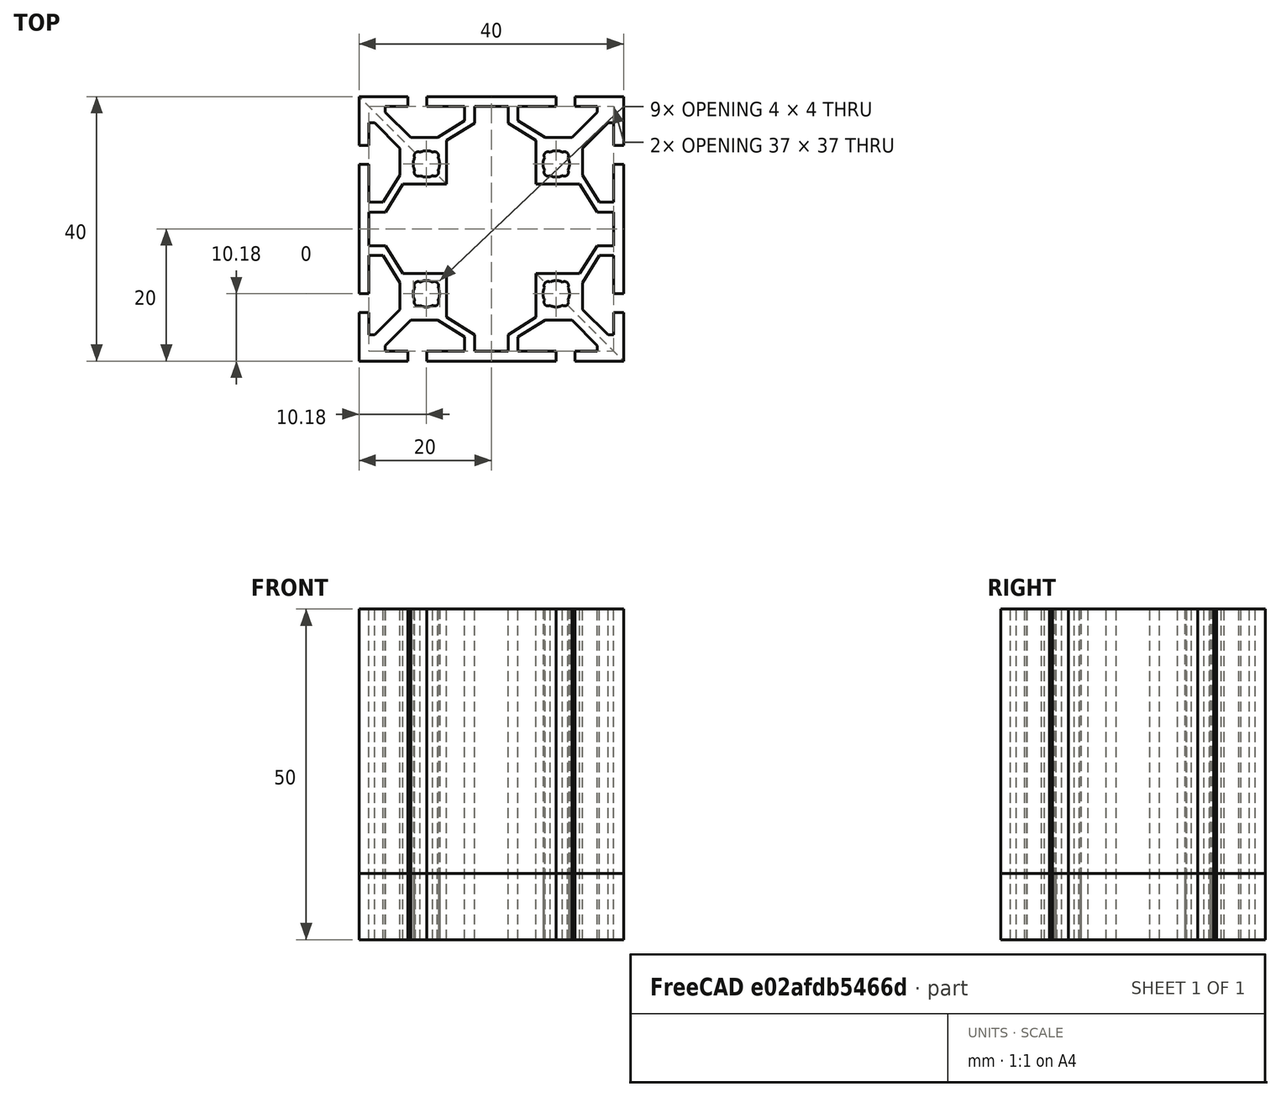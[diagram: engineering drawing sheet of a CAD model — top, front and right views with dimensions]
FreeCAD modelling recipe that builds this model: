
FCSTD DOCUMENT  (FreeCAD 0.18R16093 (Git))
Label: Profile 20-4040
License: All rights reserved
LicenseURL: http://en.wikipedia.org/wiki/All_rights_reserved
objects: PartDesign::Body×3, Sketcher::SketchObject×2, PartDesign::Pad×2, PartDesign::Mirrored×2, PartDesign::PolarPattern×1, PartDesign::FeatureBase×1, PartDesign::Boolean×1, App::Part×1
note: 14 computed .brp shape members not serialized (recipe doc carries the construction recipe); baked Part::Feature solids carry a one-line shape summary decoded from their .brp

FEATURE [Sketcher::SketchObject] Sketch
  MapMode = 5
  Support = -> [XY_Plane001]
  sketch-geometry (38):
    g0: LineSegment [constr] StartX=-22.5 StartY=-22.5 StartZ=0 EndX=22.5 EndY=-22.5 EndZ=0
    g1: LineSegment [constr] StartX=22.5 StartY=-22.5 StartZ=0 EndX=22.5 EndY=22.5 EndZ=0
    g2: LineSegment [constr] StartX=22.5 StartY=22.5 StartZ=0 EndX=-22.5 EndY=22.5 EndZ=0
    g3: LineSegment [constr] StartX=-22.5 StartY=22.5 StartZ=0 EndX=-22.5 EndY=-22.5 EndZ=0
    g4: LineSegment [constr] StartX=-22.5 StartY=22.5 StartZ=0 EndX=0 EndY=0 EndZ=0
    g5: LineSegment [constr] StartX=0 StartY=0 StartZ=0 EndX=22.5 EndY=-22.5 EndZ=0
    g6: LineSegment StartX=13.369 StartY=6.77383 StartZ=0 EndX=15.9987 EndY=2.5456 EndZ=0
    g7: LineSegment StartX=15.9987 StartY=2.5456 StartZ=0 EndX=18.5 EndY=2.5456 EndZ=0
    g8: LineSegment StartX=18.5 StartY=2.5456 StartZ=0 EndX=18.5 EndY=0 EndZ=0
    g9: LineSegment StartX=18.5 StartY=0 StartZ=0 EndX=20 EndY=0 EndZ=0
    g10: LineSegment StartX=20 StartY=0 StartZ=0 EndX=20 EndY=9.77979 EndZ=0
    g11: LineSegment StartX=20 StartY=9.77979 StartZ=0 EndX=18.5 EndY=9.77979 EndZ=0
    g12: LineSegment StartX=18.5 StartY=9.77979 StartZ=0 EndX=18.5 EndY=4.0456 EndZ=0
    g13: LineSegment StartX=18.5 StartY=4.0456 StartZ=0 EndX=16.3382 EndY=4.0456 EndZ=0
    g14: LineSegment StartX=16.3382 StartY=4.0456 StartZ=0 EndX=13.8 EndY=8.12685 EndZ=0
    g15: LineSegment StartX=13.8 StartY=8.12685 StartZ=0 EndX=13.8 EndY=12.191 EndZ=0
    g16: LineSegment StartX=13.8 StartY=12.191 StartZ=0 EndX=17.6446 EndY=16.0356 EndZ=0
    g17: LineSegment StartX=17.6446 StartY=16.0356 StartZ=0 EndX=18.5 EndY=16.0356 EndZ=0
    g18: LineSegment StartX=18.5 StartY=16.0356 StartZ=0 EndX=18.5 EndY=12.63 EndZ=0
    g19: LineSegment StartX=18.5 StartY=12.63 StartZ=0 EndX=20 EndY=12.63 EndZ=0
    g20: LineSegment StartX=20 StartY=12.63 StartZ=0 EndX=20 EndY=20 EndZ=0
    g21: LineSegment StartX=13.369 StartY=6.77383 StartZ=0 EndX=6.77383 EndY=6.77383 EndZ=0
    g22: LineSegment StartX=6.77383 StartY=6.77383 StartZ=0 EndX=8.14622 EndY=8.14622 EndZ=0
    g23: LineSegment [constr] StartX=8.57049 StartY=11.0705 StartZ=0 EndX=11.0705 EndY=11.0705 EndZ=0
    g24: LineSegment [constr] StartX=11.0705 StartY=11.0705 StartZ=0 EndX=11.0705 EndY=8.57049 EndZ=0
    g25: LineSegment [constr] StartX=11.0705 StartY=8.57049 StartZ=0 EndX=8.57049 EndY=8.57049 EndZ=0
    g26: LineSegment [constr] StartX=8.57049 StartY=8.57049 StartZ=0 EndX=8.57049 EndY=11.0705 EndZ=0
    g27: LineSegment [constr] StartX=8.57049 StartY=11.0705 StartZ=0 EndX=9.82049 EndY=9.82049 EndZ=0
    g28: LineSegment [constr] StartX=9.82049 StartY=9.82049 StartZ=0 EndX=11.0705 EndY=8.57049 EndZ=0
    g29: LineSegment StartX=11.4947 StartY=11.4947 StartZ=0 EndX=20 EndY=20 EndZ=0
    g30: LineSegment [constr] StartX=18.5 StartY=4.0456 StartZ=0 EndX=18.5 EndY=2.5456 EndZ=0
    g31: LineSegment [constr] StartX=11.4947 StartY=11.4947 StartZ=0 EndX=11.0705 EndY=11.0705 EndZ=0
    g32: LineSegment [constr] StartX=8.57049 StartY=8.57049 StartZ=0 EndX=8.14622 EndY=8.14622 EndZ=0
    g33: ArcOfCircle CenterX=11.0705 CenterY=8.57049 CenterZ=0 NormalX=0 NormalY=0 NormalZ=1 AngleXU=0 Radius=0.6 StartAngle=4.17221 EndAngle=6.82336
    g34: ArcOfCircle CenterX=8.57049 CenterY=8.57049 CenterZ=0 NormalX=0 NormalY=0 NormalZ=1 AngleXU=0 Radius=0.6 StartAngle=3.92699 EndAngle=5.25256
    g35: ArcOfCircle CenterX=11.0705 CenterY=11.0705 CenterZ=0 NormalX=0 NormalY=0 NormalZ=1 AngleXU=0 Radius=0.6 StartAngle=5.74301 EndAngle=7.06858
    g36: ArcOfCircle CenterX=9.82049 CenterY=9.82049 CenterZ=0 NormalX=0 NormalY=0 NormalZ=1 AngleXU=0 Radius=2 StartAngle=5.79309 EndAngle=6.77329
    g37: ArcOfCircle CenterX=9.82049 CenterY=9.82049 CenterZ=0 NormalX=0 NormalY=0 NormalZ=1 AngleXU=0 Radius=2 StartAngle=4.22229 EndAngle=5.20249
  constraints (99):
    c: Horizontal(g0)
    c: Coincident(g0,g1)
    c: Vertical(g1)
    c: Coincident(g1,g2)
    c: Horizontal(g2)
    c: Coincident(g2,g3)
    c: Coincident(g3,g0)
    c: Vertical(g3)
    c: Coincident(g2,g4)
    c: Coincident(g4,g-1)
    c: Coincident(g4,g5)
    c: Coincident(g5,g0)
    c: Parallel(g4,g5)
    c: Equal(g1,g2)
    c: DistanceX(g2,g2) = 45
    c: Coincident(g6,g7)
    c: Coincident(g7,g8)
    c: PointOnObject(g8,g-1)
    c: Coincident(g8,g9)
    c: PointOnObject(g9,g-1)
    c: Coincident(g9,g10)
    c: Vertical(g10)
    c: Coincident(g10,g11)
    c: Horizontal(g11)
    c: Coincident(g11,g12)
    c: Vertical(g12)
    c: Coincident(g12,g13)
    c: Coincident(g13,g14)
    c: Coincident(g14,g15)
    c: Vertical(g15)
    c: Coincident(g15,g16)
    c: Coincident(g16,g17)
    c: Coincident(g17,g18)
    c: Coincident(g18,g19)
    c: Horizontal(g19)
    c: Coincident(g19,g20)
    c: Vertical(g20)
    c: Coincident(g6,g21)
    c: Horizontal(g21)
    c: Coincident(g21,g22)
    c: Coincident(g29,g20)
    c: Coincident(g24,g25)
    c: Coincident(g26,g23)
    c: Horizontal(g23)
    c: Horizontal(g25)
    c: Vertical(g24)
    c: Vertical(g26)
    c: Coincident(g23,g27)
    c: Coincident(g27,g28)
    c: Coincident(g28,g24)
    c: Equal(g28,g27)
    c: Vertical(g18)
    c: Vertical(g8)
    c: Horizontal(g13)
    c: Horizontal(g7)
    c: Horizontal(g17)
    c: DistanceX(g-1,g20) = 20
    c: DistanceX(g14,g11) = 4.7
    c: Vertical(g12,g7)
    c: DistanceX(g9,g9) = 1.5
    c: Vertical(g19,g10)
    c: Parallel(g16,g29)
    c: Equal(g19,g9)
    c: DistanceY(g20,g20) = 7.37
    c: DistanceY(g12,g17) = 11.99
    c: Parallel(g14,g6)
    c: Coincident(g30,g12)
    c: Coincident(g30,g7)
    c: Equal(g9,g30)
    c: Coincident(g24,g23)
    c: Coincident(g26,g25)
    c: Parallel(g28,g27)
    c: Parallel(g22,g29)
    c: DistanceY(g-1,g20) = 20
    c: Coincident(g31,g23)
    c: Coincident(g32,g25)
    c: Equal(g31,g32)
    c: Parallel(g32,g22)
    c: Equal(g24,g25)
    c: Coincident(g33,g24)
    c: Coincident(g34,g25)
    c: Coincident(g35,g23)
    c: Coincident(g36,g35)
    c: Coincident(g29,g35)
    c: Coincident(g22,g34)
    c: Coincident(g29,g31)
    c: Coincident(g32,g22)
    c: Coincident(g33,g36)
    c: Equal(g33,g34)
    c: Radius(g35) = 0.6
    c: DistanceX(g25,g25) = 2.5
    c: Parallel(g31,g29)
    c: Coincident(g37,g27)
    c: Coincident(g37,g33)
    c: Coincident(g37,g34)
    c: Equal(g36,g37)
    c: Radius(g36) = 2
    c: Coincident(g37,g36)
    c: Angle(g29,g20) = 0.785398
FEATURE [PartDesign::Pad] Pad
  Length = 10
  Length2 = 100
  Profile = -> Sketch
  Refine = true
  Type = 0
FEATURE [PartDesign::Mirrored] Mirrored
  BaseFeature = -> Pad
  MirrorPlane = -> Pad [Face19]
  Originals = -> [Pad]
  Refine = true
FEATURE [PartDesign::PolarPattern] PolarPattern
  Angle = 90
  Axis = -> Sketch [N_Axis]
  BaseFeature = -> Mirrored
  Occurrences = 2
  Originals = -> [Pad]
  Refine = true
FEATURE [PartDesign::Mirrored] Mirrored001
  BaseFeature = -> PolarPattern
  MirrorPlane = -> XZ_Plane001
  Originals = -> [Pad]
  Refine = true
FEATURE [PartDesign::FeatureBase] Clone
  BaseFeature = -> Mirrored001
  Placement = pos=(0,0,0) rot=(0,0,1;3.14159rad)
FEATURE [PartDesign::Body] Body001
  BaseFeature = -> Mirrored001
  Group = -> [Clone]
  Origin = -> Origin002
  Tip = -> Clone
FEATURE [PartDesign::Boolean] Boolean
  BaseFeature = -> Mirrored001
  Group = -> [Body001]
  Refine = true
  Type = 0
FEATURE [PartDesign::Body] Body
  Group = -> [Sketch,Pad,Mirrored,PolarPattern,Mirrored001,Boolean]
  Origin = -> Origin001
  Tip = -> Boolean
FEATURE [Sketcher::SketchObject] Sketch001
  sketch-geometry (151):
    g0: LineSegment StartX=-12.63 StartY=20 StartZ=0 EndX=-20 EndY=20 EndZ=0
    g1: LineSegment StartX=-12.63 StartY=18.5 StartZ=0 EndX=-12.63 EndY=20 EndZ=0
    g2: LineSegment StartX=-16.0356 StartY=18.5 StartZ=0 EndX=-12.63 EndY=18.5 EndZ=0
    g3: LineSegment StartX=-16.0356 StartY=17.6446 StartZ=0 EndX=-16.0356 EndY=18.5 EndZ=0
    g4: LineSegment StartX=-12.191 StartY=13.8 StartZ=0 EndX=-16.0356 EndY=17.6446 EndZ=0
    g5: LineSegment StartX=-8.12685 StartY=13.8 StartZ=0 EndX=-12.191 EndY=13.8 EndZ=0
    g6: LineSegment StartX=-4.0456 StartY=16.3382 StartZ=0 EndX=-8.12685 EndY=13.8 EndZ=0
    g7: LineSegment StartX=-4.0456 StartY=18.5 StartZ=0 EndX=-4.0456 EndY=16.3382 EndZ=0
    g8: LineSegment StartX=-9.77979 StartY=18.5 StartZ=0 EndX=-4.0456 EndY=18.5 EndZ=0
    g9: LineSegment StartX=-9.77979 StartY=20 StartZ=0 EndX=-9.77979 EndY=18.5 EndZ=0
    g10: LineSegment StartX=-9.77979 StartY=20 StartZ=0 EndX=9.77979 EndY=20 EndZ=0
    g11: LineSegment StartX=9.77979 StartY=20 StartZ=0 EndX=9.77979 EndY=18.5 EndZ=0
    g12: LineSegment StartX=9.77979 StartY=18.5 StartZ=0 EndX=4.0456 EndY=18.5 EndZ=0
    g13: LineSegment StartX=4.0456 StartY=18.5 StartZ=0 EndX=4.0456 EndY=16.3382 EndZ=0
    g14: LineSegment StartX=4.0456 StartY=16.3382 StartZ=0 EndX=8.12685 EndY=13.8 EndZ=0
    g15: LineSegment StartX=8.12685 StartY=13.8 StartZ=0 EndX=12.191 EndY=13.8 EndZ=0
    g16: LineSegment StartX=12.191 StartY=13.8 StartZ=0 EndX=16.0356 EndY=17.6446 EndZ=0
    g17: LineSegment StartX=16.0356 StartY=17.6446 StartZ=0 EndX=16.0356 EndY=18.5 EndZ=0
    g18: LineSegment StartX=16.0356 StartY=18.5 StartZ=0 EndX=12.63 EndY=18.5 EndZ=0
    g19: LineSegment StartX=12.63 StartY=18.5 StartZ=0 EndX=12.63 EndY=20 EndZ=0
    g20: LineSegment StartX=12.63 StartY=20 StartZ=0 EndX=20 EndY=20 EndZ=0
    g21: LineSegment StartX=20 StartY=12.63 StartZ=0 EndX=20 EndY=20 EndZ=0
    g22: LineSegment StartX=18.5 StartY=12.63 StartZ=0 EndX=20 EndY=12.63 EndZ=0
    g23: LineSegment StartX=18.5 StartY=16.0356 StartZ=0 EndX=18.5 EndY=12.63 EndZ=0
    g24: LineSegment StartX=17.6446 StartY=16.0356 StartZ=0 EndX=18.5 EndY=16.0356 EndZ=0
    g25: LineSegment StartX=13.8 StartY=12.191 StartZ=0 EndX=17.6446 EndY=16.0356 EndZ=0
    g26: LineSegment StartX=13.8 StartY=8.12685 StartZ=0 EndX=13.8 EndY=12.191 EndZ=0
    g27: LineSegment StartX=16.3382 StartY=4.0456 StartZ=0 EndX=13.8 EndY=8.12685 EndZ=0
    g28: LineSegment StartX=18.5 StartY=4.0456 StartZ=0 EndX=16.3382 EndY=4.0456 EndZ=0
    g29: LineSegment StartX=18.5 StartY=9.77979 StartZ=0 EndX=18.5 EndY=4.0456 EndZ=0
    g30: LineSegment StartX=20 StartY=9.77979 StartZ=0 EndX=18.5 EndY=9.77979 EndZ=0
    g31: LineSegment StartX=20 StartY=9.77979 StartZ=0 EndX=20 EndY=-9.77979 EndZ=0
    g32: LineSegment StartX=20 StartY=-9.77979 StartZ=0 EndX=18.5 EndY=-9.77979 EndZ=0
    g33: LineSegment StartX=18.5 StartY=-9.77979 StartZ=0 EndX=18.5 EndY=-4.0456 EndZ=0
    g34: LineSegment StartX=18.5 StartY=-4.0456 StartZ=0 EndX=16.3382 EndY=-4.0456 EndZ=0
    g35: LineSegment StartX=16.3382 StartY=-4.0456 StartZ=0 EndX=13.8 EndY=-8.12685 EndZ=0
    g36: LineSegment StartX=13.8 StartY=-8.12685 StartZ=0 EndX=13.8 EndY=-12.191 EndZ=0
    g37: LineSegment StartX=13.8 StartY=-12.191 StartZ=0 EndX=17.6446 EndY=-16.0356 EndZ=0
    g38: LineSegment StartX=17.6446 StartY=-16.0356 StartZ=0 EndX=18.5 EndY=-16.0356 EndZ=0
    g39: LineSegment StartX=18.5 StartY=-16.0356 StartZ=0 EndX=18.5 EndY=-12.63 EndZ=0
    g40: LineSegment StartX=18.5 StartY=-12.63 StartZ=0 EndX=20 EndY=-12.63 EndZ=0
    g41: LineSegment StartX=20 StartY=-12.63 StartZ=0 EndX=20 EndY=-20 EndZ=0
    g42: LineSegment StartX=12.63 StartY=-20 StartZ=0 EndX=20 EndY=-20 EndZ=0
    g43: LineSegment StartX=12.63 StartY=-18.5 StartZ=0 EndX=12.63 EndY=-20 EndZ=0
    g44: LineSegment StartX=16.0356 StartY=-18.5 StartZ=0 EndX=12.63 EndY=-18.5 EndZ=0
    g45: LineSegment StartX=16.0356 StartY=-17.6446 StartZ=0 EndX=16.0356 EndY=-18.5 EndZ=0
    g46: LineSegment StartX=12.191 StartY=-13.8 StartZ=0 EndX=16.0356 EndY=-17.6446 EndZ=0
    g47: LineSegment StartX=8.12685 StartY=-13.8 StartZ=0 EndX=12.191 EndY=-13.8 EndZ=0
    g48: LineSegment StartX=4.0456 StartY=-16.3382 StartZ=0 EndX=8.12685 EndY=-13.8 EndZ=0
    g49: LineSegment StartX=4.0456 StartY=-18.5 StartZ=0 EndX=4.0456 EndY=-16.3382 EndZ=0
    g50: LineSegment StartX=9.77979 StartY=-18.5 StartZ=0 EndX=4.0456 EndY=-18.5 EndZ=0
    g51: LineSegment StartX=9.77979 StartY=-20 StartZ=0 EndX=9.77979 EndY=-18.5 EndZ=0
    g52: LineSegment StartX=9.77979 StartY=-20 StartZ=0 EndX=-9.77979 EndY=-20 EndZ=0
    g53: LineSegment StartX=-9.77979 StartY=-20 StartZ=0 EndX=-9.77979 EndY=-18.5 EndZ=0
    g54: LineSegment StartX=-9.77979 StartY=-18.5 StartZ=0 EndX=-4.0456 EndY=-18.5 EndZ=0
    g55: LineSegment StartX=-4.0456 StartY=-18.5 StartZ=0 EndX=-4.0456 EndY=-16.3382 EndZ=0
    g56: LineSegment StartX=-4.0456 StartY=-16.3382 StartZ=0 EndX=-8.12685 EndY=-13.8 EndZ=0
    g57: LineSegment StartX=-8.12685 StartY=-13.8 StartZ=0 EndX=-12.191 EndY=-13.8 EndZ=0
    g58: LineSegment StartX=-12.191 StartY=-13.8 StartZ=0 EndX=-16.0356 EndY=-17.6446 EndZ=0
    g59: LineSegment StartX=-16.0356 StartY=-17.6446 StartZ=0 EndX=-16.0356 EndY=-18.5 EndZ=0
    g60: LineSegment StartX=-16.0356 StartY=-18.5 StartZ=0 EndX=-12.63 EndY=-18.5 EndZ=0
    g61: LineSegment StartX=-12.63 StartY=-18.5 StartZ=0 EndX=-12.63 EndY=-20 EndZ=0
    g62: LineSegment StartX=-12.63 StartY=-20 StartZ=0 EndX=-20 EndY=-20 EndZ=0
    g63: LineSegment StartX=-20 StartY=-12.63 StartZ=0 EndX=-20 EndY=-20 EndZ=0
    g64: LineSegment StartX=-18.5 StartY=-12.63 StartZ=0 EndX=-20 EndY=-12.63 EndZ=0
    g65: LineSegment StartX=-18.5 StartY=-16.0356 StartZ=0 EndX=-18.5 EndY=-12.63 EndZ=0
    g66: LineSegment StartX=-17.6446 StartY=-16.0356 StartZ=0 EndX=-18.5 EndY=-16.0356 EndZ=0
    g67: LineSegment StartX=-13.8 StartY=-12.191 StartZ=0 EndX=-17.6446 EndY=-16.0356 EndZ=0
    g68: LineSegment StartX=-13.8 StartY=-8.12685 StartZ=0 EndX=-13.8 EndY=-12.191 EndZ=0
    g69: LineSegment StartX=-16.3382 StartY=-4.0456 StartZ=0 EndX=-13.8 EndY=-8.12685 EndZ=0
    g70: LineSegment StartX=-18.5 StartY=-4.0456 StartZ=0 EndX=-16.3382 EndY=-4.0456 EndZ=0
    g71: LineSegment StartX=-18.5 StartY=-9.77979 StartZ=0 EndX=-18.5 EndY=-4.0456 EndZ=0
    g72: LineSegment StartX=-20 StartY=-9.77979 StartZ=0 EndX=-18.5 EndY=-9.77979 EndZ=0
    g73: LineSegment StartX=-20 StartY=-9.77979 StartZ=0 EndX=-20 EndY=9.77979 EndZ=0
    g74: LineSegment StartX=-20 StartY=9.77979 StartZ=0 EndX=-18.5 EndY=9.77979 EndZ=0
    g75: LineSegment StartX=-18.5 StartY=9.77979 StartZ=0 EndX=-18.5 EndY=4.0456 EndZ=0
    g76: LineSegment StartX=-18.5 StartY=4.0456 StartZ=0 EndX=-16.3382 EndY=4.0456 EndZ=0
    g77: LineSegment StartX=-16.3382 StartY=4.0456 StartZ=0 EndX=-13.8 EndY=8.12685 EndZ=0
    g78: LineSegment StartX=-13.8 StartY=8.12685 StartZ=0 EndX=-13.8 EndY=12.191 EndZ=0
    g79: LineSegment StartX=-13.8 StartY=12.191 StartZ=0 EndX=-17.6446 EndY=16.0356 EndZ=0
    g80: LineSegment StartX=-17.6446 StartY=16.0356 StartZ=0 EndX=-18.5 EndY=16.0356 EndZ=0
    g81: LineSegment StartX=-18.5 StartY=16.0356 StartZ=0 EndX=-18.5 EndY=12.63 EndZ=0
    g82: LineSegment StartX=-18.5 StartY=12.63 StartZ=0 EndX=-20 EndY=12.63 EndZ=0
    g83: LineSegment StartX=-20 StartY=12.63 StartZ=0 EndX=-20 EndY=20 EndZ=0
    g84: LineSegment StartX=-13.369 StartY=-6.77383 StartZ=0 EndX=-6.77383 EndY=-6.77383 EndZ=0
    g85: LineSegment StartX=-6.77383 StartY=-13.369 StartZ=0 EndX=-6.77383 EndY=-6.77383 EndZ=0
    g86: LineSegment StartX=-6.77383 StartY=-13.369 StartZ=0 EndX=-2.5456 EndY=-15.9987 EndZ=0
    g87: LineSegment StartX=-2.5456 StartY=-15.9987 StartZ=0 EndX=-2.5456 EndY=-18.5 EndZ=0
    g88: LineSegment StartX=2.5456 StartY=-18.5 StartZ=0 EndX=-2.5456 EndY=-18.5 EndZ=0
    g89: LineSegment StartX=2.5456 StartY=-15.9987 StartZ=0 EndX=2.5456 EndY=-18.5 EndZ=0
    g90: LineSegment StartX=6.77383 StartY=-13.369 StartZ=0 EndX=2.5456 EndY=-15.9987 EndZ=0
    g91: LineSegment StartX=6.77383 StartY=-13.369 StartZ=0 EndX=6.77383 EndY=-6.77383 EndZ=0
    g92: LineSegment StartX=13.369 StartY=6.77383 StartZ=0 EndX=6.77383 EndY=6.77383 EndZ=0
    g93: LineSegment StartX=13.369 StartY=6.77383 StartZ=0 EndX=15.9987 EndY=2.5456 EndZ=0
    g94: LineSegment StartX=6.77383 StartY=13.369 StartZ=0 EndX=6.77383 EndY=6.77383 EndZ=0
    g95: LineSegment StartX=15.9987 StartY=2.5456 StartZ=0 EndX=18.5 EndY=2.5456 EndZ=0
    g96: LineSegment StartX=6.77383 StartY=13.369 StartZ=0 EndX=2.5456 EndY=15.9987 EndZ=0
    g97: LineSegment StartX=2.5456 StartY=15.9987 StartZ=0 EndX=2.5456 EndY=18.5 EndZ=0
    g98: LineSegment StartX=-2.5456 StartY=18.5 StartZ=0 EndX=2.5456 EndY=18.5 EndZ=0
    g99: LineSegment StartX=-2.5456 StartY=15.9987 StartZ=0 EndX=-2.5456 EndY=18.5 EndZ=0
    g100: LineSegment StartX=-6.77383 StartY=13.369 StartZ=0 EndX=-2.5456 EndY=15.9987 EndZ=0
    g101: LineSegment StartX=-6.77383 StartY=13.369 StartZ=0 EndX=-6.77383 EndY=6.77383 EndZ=0
    g102: LineSegment StartX=18.5 StartY=2.5456 StartZ=0 EndX=18.5 EndY=-2.5456 EndZ=0
    g103: LineSegment StartX=13.369 StartY=-6.77383 StartZ=0 EndX=6.77383 EndY=-6.77383 EndZ=0
    g104: LineSegment StartX=13.369 StartY=-6.77383 StartZ=0 EndX=15.9987 EndY=-2.5456 EndZ=0
    g105: LineSegment StartX=15.9987 StartY=-2.5456 StartZ=0 EndX=18.5 EndY=-2.5456 EndZ=0
    g106: LineSegment StartX=-13.369 StartY=6.77383 StartZ=0 EndX=-6.77383 EndY=6.77383 EndZ=0
    g107: LineSegment StartX=-13.369 StartY=6.77383 StartZ=0 EndX=-15.9987 EndY=2.5456 EndZ=0
    g108: LineSegment StartX=-15.9987 StartY=2.5456 StartZ=0 EndX=-18.5 EndY=2.5456 EndZ=0
    g109: LineSegment StartX=-18.5 StartY=-2.5456 StartZ=0 EndX=-18.5 EndY=2.5456 EndZ=0
    g110: LineSegment StartX=-15.9987 StartY=-2.5456 StartZ=0 EndX=-18.5 EndY=-2.5456 EndZ=0
    g111: LineSegment StartX=-13.369 StartY=-6.77383 StartZ=0 EndX=-15.9987 EndY=-2.5456 EndZ=0
    g112: ArcOfCircle CenterX=-8.57049 CenterY=-8.57049 CenterZ=0 NormalX=0 NormalY=0 NormalZ=1 AngleXU=-1.5708 Radius=0.6 StartAngle=1.03062 EndAngle=2.35619
    g113: ArcOfCircle CenterX=-8.57049 CenterY=-8.57049 CenterZ=0 NormalX=0 NormalY=0 NormalZ=1 AngleXU=3.14159 Radius=0.6 StartAngle=3.92699 EndAngle=5.25256
    g114: ArcOfCircle CenterX=-10 CenterY=-9.99052 CenterZ=0 NormalX=0 NormalY=0 NormalZ=1 AngleXU=3.14159 Radius=2.095 StartAngle=4.1766 EndAngle=5.06528
    g115: ArcOfCircle CenterX=-11.0705 CenterY=-8.57049 CenterZ=0 NormalX=0 NormalY=0 NormalZ=1 AngleXU=3.14159 Radius=0.6 StartAngle=4.17221 EndAngle=6.82336
    g116: ArcOfCircle CenterX=-10 CenterY=-9.99052 CenterZ=0 NormalX=0 NormalY=0 NormalZ=1 AngleXU=3.14159 Radius=2.095 StartAngle=5.75099 EndAngle=6.68341
    g117: ArcOfCircle CenterX=-11.0705 CenterY=-11.0705 CenterZ=0 NormalX=0 NormalY=0 NormalZ=1 AngleXU=-1.5708 Radius=0.6 StartAngle=5.49779 EndAngle=6.82336
    g118: ArcOfCircle CenterX=-11.0705 CenterY=-11.0705 CenterZ=0 NormalX=0 NormalY=0 NormalZ=1 AngleXU=3.14159 Radius=0.6 StartAngle=5.74301 EndAngle=7.06858
    g119: ArcOfCircle CenterX=-10 CenterY=-9.99052 CenterZ=0 NormalX=0 NormalY=0 NormalZ=1 AngleXU=-1.5708 Radius=2.095 StartAngle=5.89427 EndAngle=6.88085
    g120: ArcOfCircle CenterX=-8.57049 CenterY=-11.0705 CenterZ=0 NormalX=0 NormalY=0 NormalZ=1 AngleXU=-1.5708 Radius=0.6 StartAngle=5.74301 EndAngle=8.39416
    g121: ArcOfCircle CenterX=-10 CenterY=-9.99052 CenterZ=0 NormalX=0 NormalY=0 NormalZ=1 AngleXU=-1.5708 Radius=2.095 StartAngle=1.1689 EndAngle=2.10217
    g122: ArcOfCircle CenterX=10 CenterY=-9.99052 CenterZ=0 NormalX=0 NormalY=0 NormalZ=1 AngleXU=0 Radius=2.095 StartAngle=5.88179 EndAngle=6.81528
    g123: ArcOfCircle CenterX=11.0705 CenterY=-8.57049 CenterZ=0 NormalX=0 NormalY=0 NormalZ=1 AngleXU=0 Radius=0.6 StartAngle=5.74301 EndAngle=8.39416
    g124: ArcOfCircle CenterX=10 CenterY=-9.99052 CenterZ=0 NormalX=0 NormalY=0 NormalZ=1 AngleXU=0 Radius=2.095 StartAngle=1.21703 EndAngle=2.10532
    g125: ArcOfCircle CenterX=10 CenterY=-9.99052 CenterZ=0 NormalX=0 NormalY=0 NormalZ=1 AngleXU=-1.5708 Radius=2.095 StartAngle=4.17839 EndAngle=5.11082
    g126: ArcOfCircle CenterX=8.57049 CenterY=-11.0705 CenterZ=0 NormalX=0 NormalY=0 NormalZ=1 AngleXU=-1.5708 Radius=0.6 StartAngle=4.17221 EndAngle=6.82336
    g127: ArcOfCircle CenterX=10 CenterY=-9.99052 CenterZ=0 NormalX=0 NormalY=0 NormalZ=1 AngleXU=-1.5708 Radius=2.095 StartAngle=5.69299 EndAngle=6.679
    g128: ArcOfCircle CenterX=-10 CenterY=9.99052 CenterZ=0 NormalX=0 NormalY=0 NormalZ=1 AngleXU=1.5708 Radius=2.095 StartAngle=4.09788 EndAngle=5.3269
    g129: ArcOfCircle CenterX=-8.80803 CenterY=11.4089 CenterZ=0 NormalX=0 NormalY=0 NormalZ=1 AngleXU=1.5708 Radius=0.560775 StartAngle=4.32757 EndAngle=6.84106
    g130: ArcOfCircle CenterX=-10 CenterY=9.99052 CenterZ=0 NormalX=0 NormalY=0 NormalZ=1 AngleXU=1.5708 Radius=2.095 StartAngle=5.84173 EndAngle=6.72464
    g131: ArcOfCircle CenterX=-10 CenterY=9.99052 CenterZ=0 NormalX=0 NormalY=0 NormalZ=1 AngleXU=3.14159 Radius=2.095 StartAngle=5.66867 EndAngle=6.8977
    g132: ArcOfCircle CenterX=-11.192 CenterY=8.57212 CenterZ=0 NormalX=0 NormalY=0 NormalZ=1 AngleXU=3.14159 Radius=0.560775 StartAngle=5.89837 EndAngle=8.41185
    g133: ArcOfCircle CenterX=-10 CenterY=9.99052 CenterZ=0 NormalX=0 NormalY=0 NormalZ=1 AngleXU=3.14159 Radius=2.095 StartAngle=1.12934 EndAngle=2.01225
    g134: ArcOfCircle CenterX=8.57049 CenterY=8.57049 CenterZ=0 NormalX=0 NormalY=0 NormalZ=1 AngleXU=1.5708 Radius=0.6 StartAngle=1.03062 EndAngle=2.35619
    g135: ArcOfCircle CenterX=8.57049 CenterY=8.57049 CenterZ=0 NormalX=0 NormalY=0 NormalZ=1 AngleXU=0 Radius=0.6 StartAngle=3.92699 EndAngle=5.25256
    g136: ArcOfCircle CenterX=10 CenterY=9.99052 CenterZ=0 NormalX=0 NormalY=0 NormalZ=1 AngleXU=0 Radius=2.095 StartAngle=4.1934 EndAngle=5.06981
    g137: ArcOfCircle CenterX=11.0705 CenterY=8.57049 CenterZ=0 NormalX=0 NormalY=0 NormalZ=1 AngleXU=0 Radius=0.6 StartAngle=4.17221 EndAngle=6.82336
    g138: ArcOfCircle CenterX=10 CenterY=9.99052 CenterZ=0 NormalX=0 NormalY=0 NormalZ=1 AngleXU=0 Radius=2.095 StartAngle=5.75882 EndAngle=7.00748
    g139: ArcOfCircle CenterX=11.0338 CenterY=11.3858 CenterZ=0 NormalX=0 NormalY=0 NormalZ=1 AngleXU=1.5708 Radius=0.535322 StartAngle=4.69913 EndAngle=6.59188
    g140: ArcOfCircle CenterX=10 CenterY=9.99052 CenterZ=0 NormalX=0 NormalY=0 NormalZ=1 AngleXU=1.5708 Radius=2.095 StartAngle=5.85433 EndAngle=6.84603
    g141: ArcOfCircle CenterX=8.57229 CenterY=11.2507 CenterZ=0 NormalX=0 NormalY=0 NormalZ=1 AngleXU=1.5708 Radius=0.598104 StartAngle=5.73866 EndAngle=8.39215
    g142: ArcOfCircle CenterX=10 CenterY=9.99052 CenterZ=0 NormalX=0 NormalY=0 NormalZ=1 AngleXU=1.5708 Radius=2.095 StartAngle=1.15965 EndAngle=2.09059
    g143: ArcOfCircle CenterX=8.57049 CenterY=-8.57049 CenterZ=0 NormalX=0 NormalY=0 NormalZ=1 AngleXU=0 Radius=0.6 StartAngle=1.03062 EndAngle=2.35619
    g144: ArcOfCircle CenterX=11.0705 CenterY=-11.0705 CenterZ=0 NormalX=0 NormalY=0 NormalZ=1 AngleXU=0 Radius=0.6 StartAngle=5.49779 EndAngle=6.82336
    g145: ArcOfCircle CenterX=11.0705 CenterY=-11.0705 CenterZ=0 NormalX=0 NormalY=0 NormalZ=1 AngleXU=-1.5708 Radius=0.6 StartAngle=5.74301 EndAngle=7.06858
    g146: ArcOfCircle CenterX=8.57049 CenterY=-8.57049 CenterZ=0 NormalX=0 NormalY=0 NormalZ=1 AngleXU=-1.5708 Radius=0.6 StartAngle=3.92699 EndAngle=5.25256
    g147: ArcOfCircle CenterX=-8.80803 CenterY=8.57212 CenterZ=0 NormalX=0 NormalY=0 NormalZ=1 AngleXU=1.5708 Radius=0.560775 StartAngle=2.58372 EndAngle=5.09721
    g148: ArcOfCircle CenterX=-11.192 CenterY=11.4089 CenterZ=0 NormalX=0 NormalY=0 NormalZ=1 AngleXU=3.14159 Radius=0.560775 StartAngle=4.15452 EndAngle=6.668
    g149: LineSegment [constr] StartX=-11.192 StartY=11.4089 StartZ=0 EndX=-10 EndY=9.99052 EndZ=0
    g150: LineSegment [constr] StartX=-8.80803 StartY=8.57212 StartZ=0 EndX=-10 EndY=9.99052 EndZ=0
  constraints (71):
    c: Symmetric(g98,g97,g-2)
    c: Vertical(g99)
    c: Vertical(g97)
    c: Symmetric(g0,g20,g-2)
    c: Symmetric(g0,g62,g-1)
    c: Symmetric(g20,g41,g-1)
    c: DistanceX(g0,g20) = 40
    c: Equal(g20,g21)
    c: Equal(g21,g41)
    c: Equal(g41,g42)
    c: Equal(g42,g62)
    c: Equal(g62,g63)
    c: Equal(g63,g83)
    c: Equal(g83,g0)
    c: DistanceX(g20,g20) = 7.37
    c: DistanceX(g128,g136) = 20
    c: Coincident(g130,g128)
    c: Coincident(g136,g138)
    c: Radius(g128) = 2.095
    c: Equal(g130,g128)
    c: Equal(g128,g133)
    c: Equal(g133,g131)
    c: Equal(g131,g140)
    c: Equal(g140,g138)
    c: Equal(g138,g136)
    c: Equal(g136,g142)
    c: Equal(g142,g124)
    c: Equal(g124,g122)
    c: Equal(g122,g127)
    c: Equal(g127,g125)
    c: Equal(g125,g121)
    c: Equal(g121,g119)
    c: Equal(g119,g116)
    c: Equal(g116,g114)
    c: Coincident(g130,g148)
    c: Coincident(g128,g133)
    c: Coincident(g128,g131)
    c: Symmetric(g128,g136,g-2)
    c: Coincident(g142,g136)
    c: Coincident(g142,g140)
    c: Coincident(g114,g116)
    c: Coincident(g114,g121)
    c: Coincident(g114,g119)
    c: Coincident(g122,g127)
    c: Coincident(g122,g125)
    c: Coincident(g122,g124)
    c: Symmetric(g122,g136,g-1)
    c: Symmetric(g114,g128,g-1)
    c: Coincident(g148,g131)
    c: Coincident(g130,g129)
    c: Coincident(g129,g128)
    c: Coincident(g147,g128)
    c: Coincident(g147,g133)
    c: Coincident(g132,g133)
    c: Coincident(g131,g132)
    c: Equal(g147,g129)
    c: Equal(g129,g148)
    c: Equal(g148,g132)
    c: Horizontal(g147,g132)
    c: Horizontal(g148,g129)
    c: Equal(g150,g149)
    c: Coincident(g149,g148)
    c: Coincident(g149,g150)
    c: Coincident(g128,g149)
    c: Coincident(g150,g147)
    c: Parallel(g150,g149)
    c: Vertical(g129,g147)
    c: Vertical(g148,g132)
    c: Coincident(g140,g141)
    c: Coincident(g139,g140)
    c: Coincident(g138,g139)
FEATURE [PartDesign::Pad] Pad001
  Length = 50
  Length2 = 100
  Profile = -> Sketch001
  Refine = true
  Type = 0
FEATURE [PartDesign::Body] Body002
  Group = -> [Sketch001,Pad001]
  Origin = -> Origin003
  Tip = -> Pad001
FEATURE [App::Part] Part
  Group = -> [Body,Body002]
  Origin = -> Origin
